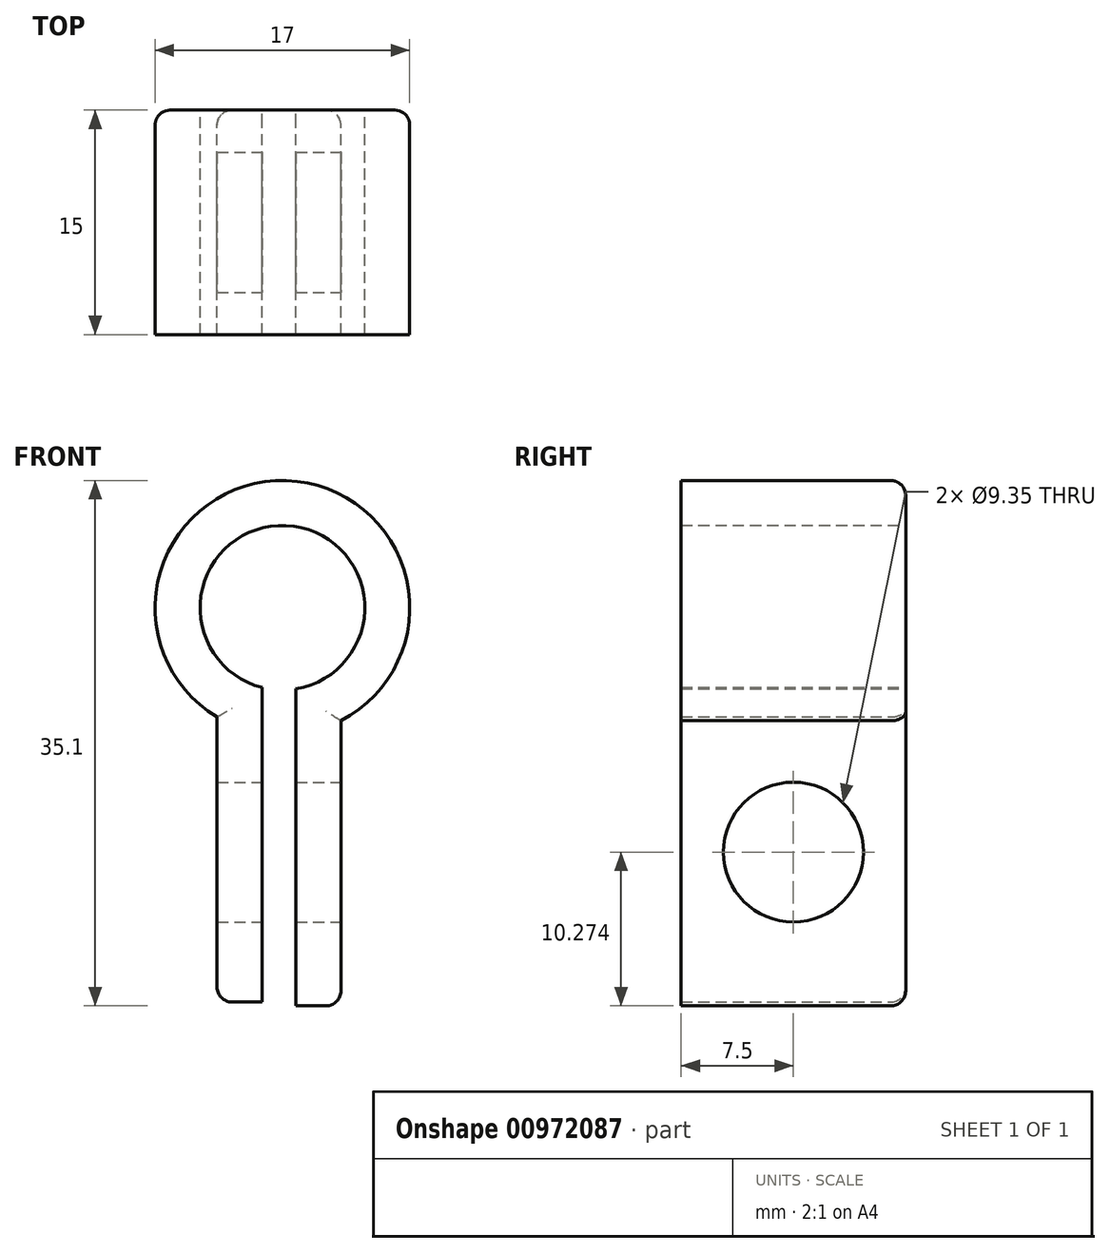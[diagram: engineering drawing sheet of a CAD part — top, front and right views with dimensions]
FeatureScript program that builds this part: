
annotation { "Feature Type Name" : "Feature", "Feature Type Description" : "" }
export const myFeature = defineFeature(function(context is Context, id is Id, definition is map)
    precondition{}
    {
        {
            var Q0;
            Q0=qCreatedBy(makeId("Front.planeOp"),FACE);
            var sketch = newSketch(context, id + "F0", { "sketchPlane" : qUnion([Q0])});
            skArc(sketch, "E0", {"start": v(0.9, -5.43) * mm, "mid": v(0.23, 5.5) * mm, "end": v(-1.36, -5.33) * mm});
            skArc(sketch, "E1", {"start": v(3.9, -7.55) * mm, "mid": v(0.26, 8.5) * mm, "end": v(-4.36, -7.3) * mm});
            skLineSegment(sketch, "E2.top", {"start": v(0.9, -26.6) * mm, "end": v(3.9, -26.6) * mm});
            skLineSegment(sketch, "E2.left", {"start": v(0.9, -5.43) * mm, "end": v(0.9, -26.6) * mm});
            skLineSegment(sketch, "E2.right", {"start": v(3.9, -7.55) * mm, "end": v(3.9, -26.6) * mm});
            skLineSegment(sketch, "E3.top", {"start": v(-1.36, -26.34) * mm, "end": v(-4.36, -26.34) * mm});
            skLineSegment(sketch, "E3.left", {"start": v(-1.36, -5.33) * mm, "end": v(-1.36, -26.34) * mm});
            skLineSegment(sketch, "E3.right", {"start": v(-4.36, -7.3) * mm, "end": v(-4.36, -26.34) * mm});
            skSolve(sketch);
        }
        {
            var Q0;
            Q0=qSketchRegion(id+"F0",true);
            extrude(context, id + "F1", {"entities" : qUnion([Q0]), "depth" : 15 * mm, "offsetDistance" : 25 * mm});
        }
        {
            var Q0;
            Q0=makeQuery(id+"F1.opExtrude","SWEPT_FACE",FACE,{"disambiguationData":[OSD([sQuery(id+"F0.wireOp",EDGE,"E2.right")])]});
            var sketch = newSketch(context, id + "F2", { "sketchPlane" : qUnion([Q0])});
            skCircle(sketch, "E4", {"center": v(-7.5, -16.33) * mm, "radius": 4.67 * mm});
            skPoint(sketch, "E4.centerSnap0", {"position": v(-7.5, -7.55) * mm});
            skSolve(sketch);
        }
        {
            var Q0;
            Q0=qSketchRegion(id+"F2",true);
            extrude(context, id + "F3", {"entities" : qUnion([Q0]), "operationType" : NewBodyOperationType.REMOVE, "endBound" : BoundingType.SYMMETRIC, "oppositeDirection" : true, "depth" : 59.6 * mm, "offsetDistance" : 25 * mm});
        }
        {
            var Q0;
            Q0=makeQuery(id+"F1.opExtrude","CAP_EDGE",EDGE,{"disambiguationData":[OSD([sQuery(id+"F0.wireOp",EDGE,"E3.right")])],"isStart":true});
            var Q1;
            Q1=makeQuery(id+"F1.opExtrude","CAP_EDGE",EDGE,{"disambiguationData":[OSD([sQuery(id+"F0.wireOp",EDGE,"E1")])],"isStart":true});
            var Q2;
            Q2=makeQuery(id+"F1.opExtrude","CAP_EDGE",EDGE,{"disambiguationData":[OSD([sQuery(id+"F0.wireOp",EDGE,"E2.right")])],"isStart":true});
            var Q3;
            Q3=makeQuery(id+"F1.opExtrude","CAP_EDGE",EDGE,{"disambiguationData":[OSD([sQuery(id+"F0.wireOp",EDGE,"E2.top")])],"isStart":true});
            var Q4;
            Q4=makeQuery(id+"F1.opExtrude","CAP_EDGE",EDGE,{"disambiguationData":[OSD([sQuery(id+"F0.wireOp",EDGE,"E3.top")])],"isStart":true});
            var Q5;
            Q5=makeQuery(id+"F1.opExtrude","SWEPT_EDGE",EDGE,{"disambiguationData":[OSD([sQuery(id+"F0.wireOp",EDGE,"E2.top"),sQuery(id+"F0.wireOp",EDGE,"E2.right")])]});
            var Q6;
            Q6=makeQuery(id+"F1.opExtrude","SWEPT_EDGE",EDGE,{"disambiguationData":[OSD([sQuery(id+"F0.wireOp",EDGE,"E3.top"),sQuery(id+"F0.wireOp",EDGE,"E3.right")])]});
            fillet(context, id + "F4", {"entities" : qUnion([Q0, Q1, Q2, Q3, Q4, Q5, Q6]), "radius" : 1 * mm, "tangentPropagation" : true, "allowEdgeOverflow" : false});
        }
    });
